# Revit family: BUILDMAT-SNA0022-Theo-1200-Drainboard-Stainless-Steel
name_source: partatom
category: Plumbing Fixtures
units: mm (PartAtom-declared; Revit-internal decimal feet)

## family parameters
Cut with Voids When Loaded = No
Host = Face
Maintain Annotation Orientation = No
Part Type = Normal
Room Calculation Point = No
Round Connector Dimension = Use Diameter
Shared = No

## types (1)
- Theo 1200 Stainless Steel
    Bracket 1 = Yes
    Bracket 2 = Yes
    Bracket 3 = Yes
    Bracket 4 = Yes
    Brand = Alma
    D. Bracket 1 = 100 mm  [stored 0.328084 ft]
    D. Bracket 2 = 50 mm  [stored 0.164042 ft]
    D. Bracket 3 = 50 mm  [stored 0.164042 ft]
    D. Bracket 4 = 50 mm  [stored 0.164042 ft]
    D. S. Pad 1 = 200 mm  [stored 0.656168 ft]
    D. S. Pad 2 = 175 mm  [stored 0.574147 ft]
    Default Elevation = 1200 mm
    Depth = 205 mm
    Description = Theo 1200x500 Double Bowl with Drain Board Sink
    Drain Sound Pad 1 = Yes
    Drain Sound Pad 2 = Yes
    Drainboard Length = 380 mm
    Gap = 70 mm  [stored 0.229659 ft]
    Length = 450 mm  [stored 1.47638 ft]
    Manufacturer = BUILDMAT
    Material = ALMA Stainless Steel
    Model = SNA0022
    Sound Pad 1 = Yes
    Sound Pad 2 = Yes
    URL = https://www.buildmat.com.au
    Width 1 = 350 mm  [stored 1.14829 ft]
    Width 2 = 350 mm  [stored 1.14829 ft]

note: [stored X ft] marks values corroborated as IEEE doubles in the binary element streams (Revit-internal decimal feet)

## geometry (parser evidence)
native form markers: Sweep x8
no freeform markers — native parametric forms only
